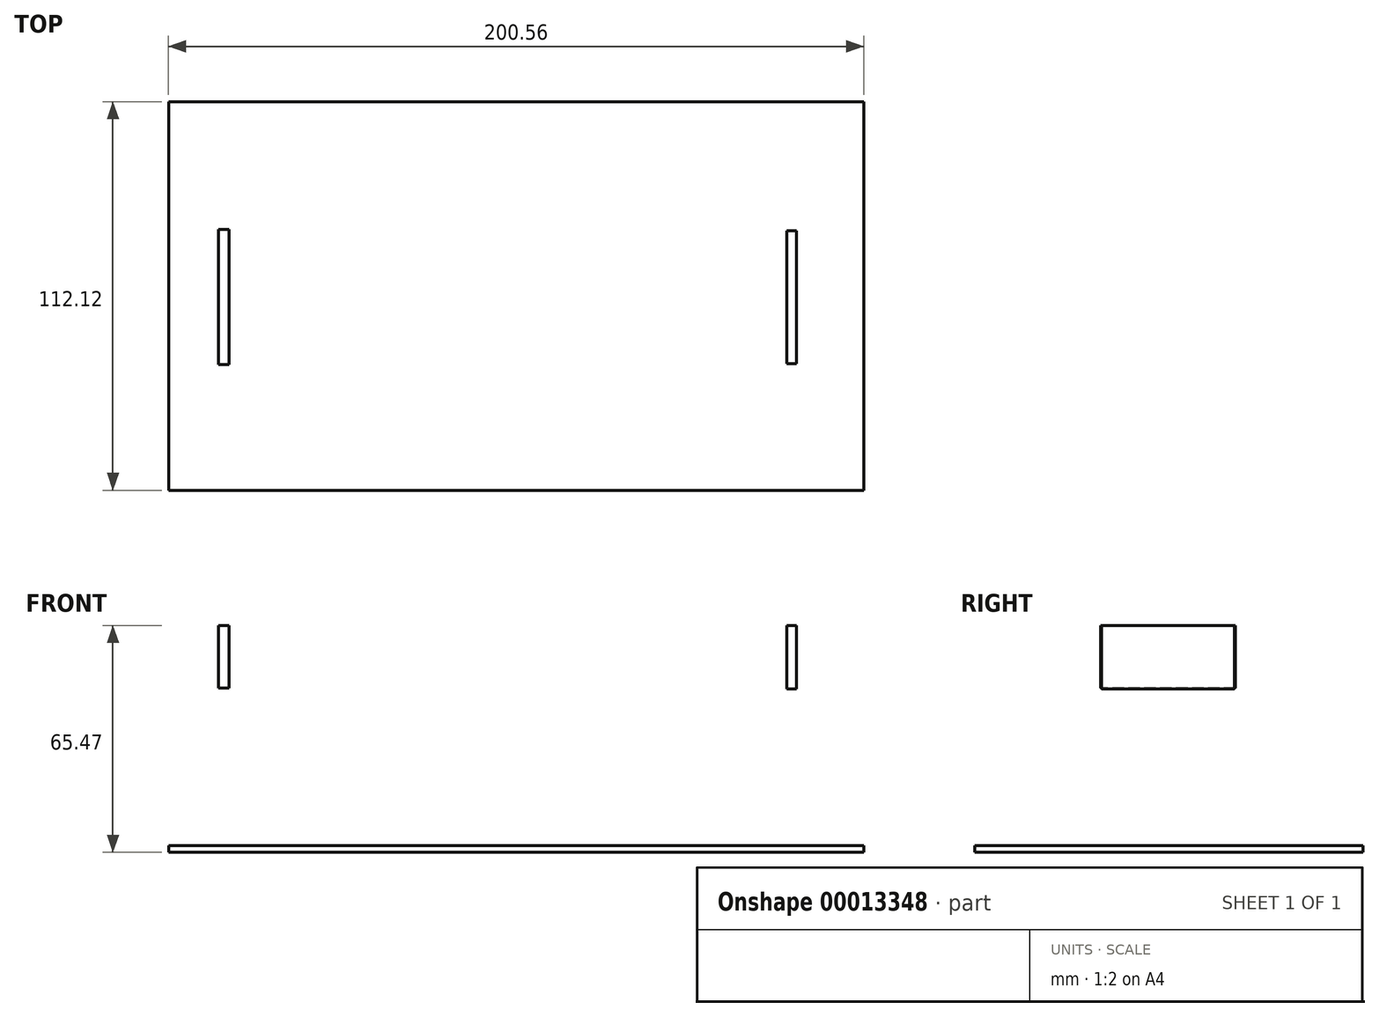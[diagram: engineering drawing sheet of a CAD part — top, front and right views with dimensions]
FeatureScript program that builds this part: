
annotation { "Feature Type Name" : "Feature", "Feature Type Description" : "" }
export const myFeature = defineFeature(function(context is Context, id is Id, definition is map)
    precondition{}
    {
        {
            var Q0;
            Q0=qCreatedBy(makeId("Top.planeOp"),FACE);
            var sketch = newSketch(context, id + "F0", { "sketchPlane" : qUnion([Q0])});
            skLineSegment(sketch, "E0.bottom", {"start": v(-100.28, 56.32) * mm, "end": v(100.28, 56.32) * mm});
            skLineSegment(sketch, "E0.top", {"start": v(-100.28, -55.8) * mm, "end": v(100.28, -55.8) * mm});
            skLineSegment(sketch, "E0.left", {"start": v(-100.28, 56.32) * mm, "end": v(-100.28, -55.8) * mm});
            skLineSegment(sketch, "E0.right", {"start": v(100.28, 56.32) * mm, "end": v(100.28, -55.8) * mm});
            skSolve(sketch);
        }
        {
            var Q0;
            Q0 = qSketchRegion(id + "F0", true);
            extrude(context, id + "F1", {"entities" : qUnion([Q0]), "depth" : 1.95 * mm});
        }
        {
            var Q0;
            Q0=makeQuery(id+"F1.opExtrude","CAP_FACE",FACE,{"disambiguationData":[OSD([sQuery(id+"F0.wireOp",EDGE,"E0.bottom"),sQuery(id+"F0.wireOp",EDGE,"E0.top"),sQuery(id+"F0.wireOp",EDGE,"E0.left"),sQuery(id+"F0.wireOp",EDGE,"E0.right")])],"isStart":false});
            var sketch = newSketch(context, id + "F2", { "sketchPlane" : qUnion([Q0])});
            skCircle(sketch, "E1", {"center": v(-90.01, 0) * mm, "radius": 4.25 * mm});
            skCircle(sketch, "E2", {"center": v(83.96, -0.53) * mm, "radius": 4.25 * mm});
            skSolve(sketch);
        }
        {
            var Q0;
            Q0=sQuery(id+"F2.wireOp",EDGE,"E2");
            var Q1;
            Q1=sQuery(id+"F2.wireOp",EDGE,"E1");
            extrude(context, id + "F3", {"bodyType" : ToolBodyType.SURFACE, "surfaceEntities" : qUnion([Q0, Q1]), "depth" : 67.58 * mm});
        }
        {
            var Q0;
            Q0=makeQuery(id+"F1.opExtrude","CAP_FACE",FACE,{"disambiguationData":[OSD([sQuery(id+"F0.wireOp",EDGE,"E0.bottom"),sQuery(id+"F0.wireOp",EDGE,"E0.top"),sQuery(id+"F0.wireOp",EDGE,"E0.left"),sQuery(id+"F0.wireOp",EDGE,"E0.right")])],"isStart":false});
            var sketch = newSketch(context, id + "F4", { "sketchPlane" : qUnion([Q0])});
            skSolve(sketch);
        }
        {
            var Q0;
            Q0=qCreatedBy(makeId("Right.planeOp"),FACE);
            var sketch = newSketch(context, id + "F5", { "sketchPlane" : qUnion([Q0])});
            skLineSegment(sketch, "E3.bottom", {"start": v(19.14, 65.47) * mm, "end": v(-19.24, 65.47) * mm});
            skLineSegment(sketch, "E3.top", {"start": v(19.14, 47.12) * mm, "end": v(-19.24, 47.12) * mm});
            skLineSegment(sketch, "E3.left", {"start": v(19.14, 65.47) * mm, "end": v(19.14, 47.12) * mm});
            skLineSegment(sketch, "E3.right", {"start": v(-19.24, 65.47) * mm, "end": v(-19.24, 47.12) * mm});
            skSolve(sketch);
        }
        {
            var Q0;
            Q0 = qSketchRegion(id + "F5", true);
            extrude(context, id + "F6", {"entities" : qUnion([Q0]), "depth" : 80.87 * mm, "hasSecondDirection" : true, "secondDirectionOppositeDirection" : false, "secondDirectionDepth" : 78.04 * mm});
        }
        {
            var Q0;
            Q0=qCreatedBy(makeId("Right.planeOp"),FACE);
            var sketch = newSketch(context, id + "F7", { "sketchPlane" : qUnion([Q0])});
            skLineSegment(sketch, "E4.bottom", {"start": v(19.46, 65.47) * mm, "end": v(-19.47, 65.47) * mm});
            skLineSegment(sketch, "E4.top", {"start": v(19.46, 47.4) * mm, "end": v(-19.47, 47.4) * mm});
            skLineSegment(sketch, "E4.left", {"start": v(19.46, 65.47) * mm, "end": v(19.46, 47.4) * mm});
            skLineSegment(sketch, "E4.right", {"start": v(-19.47, 65.47) * mm, "end": v(-19.47, 47.4) * mm});
            skSolve(sketch);
        }
        {
            var Q0;
            Q0 = qSketchRegion(id + "F7", true);
            extrude(context, id + "F8", {"entities" : qUnion([Q0]), "oppositeDirection" : true, "depth" : 85.92 * mm, "hasSecondDirection" : true, "secondDirectionOppositeDirection" : true, "secondDirectionDepth" : 82.8 * mm});
        }
        {
            var Q0;
            Q0=qCreatedBy(makeId("Top.planeOp"),FACE);
            var sketch = newSketch(context, id + "F9", { "sketchPlane" : qUnion([Q0])});
            skCircle(sketch, "E5", {"center": v(-75.77, 0) * mm, "radius": 7.5 * mm});
            skCircle(sketch, "E6", {"center": v(68.94, 0.34) * mm, "radius": 7.85 * mm});
            skSolve(sketch);
        }
        {
            var Q0;
            Q0=sQuery(id+"F9.wireOp",EDGE,"E5");
            extrude(context, id + "F10", {"bodyType" : ToolBodyType.SURFACE, "surfaceEntities" : qUnion([Q0]), "depth" : 54.58 * mm, "hasSecondDirection" : true, "secondDirectionOppositeDirection" : false, "secondDirectionDepth" : 50.25 * mm});
        }
        {
            var Q0;
            Q0=sQuery(id+"F9.wireOp",EDGE,"E6");
            extrude(context, id + "F11", {"bodyType" : ToolBodyType.SURFACE, "surfaceEntities" : qUnion([Q0]), "depth" : 55.1 * mm, "hasSecondDirection" : true, "secondDirectionOppositeDirection" : false, "secondDirectionDepth" : 50.88 * mm});
        }
    });
